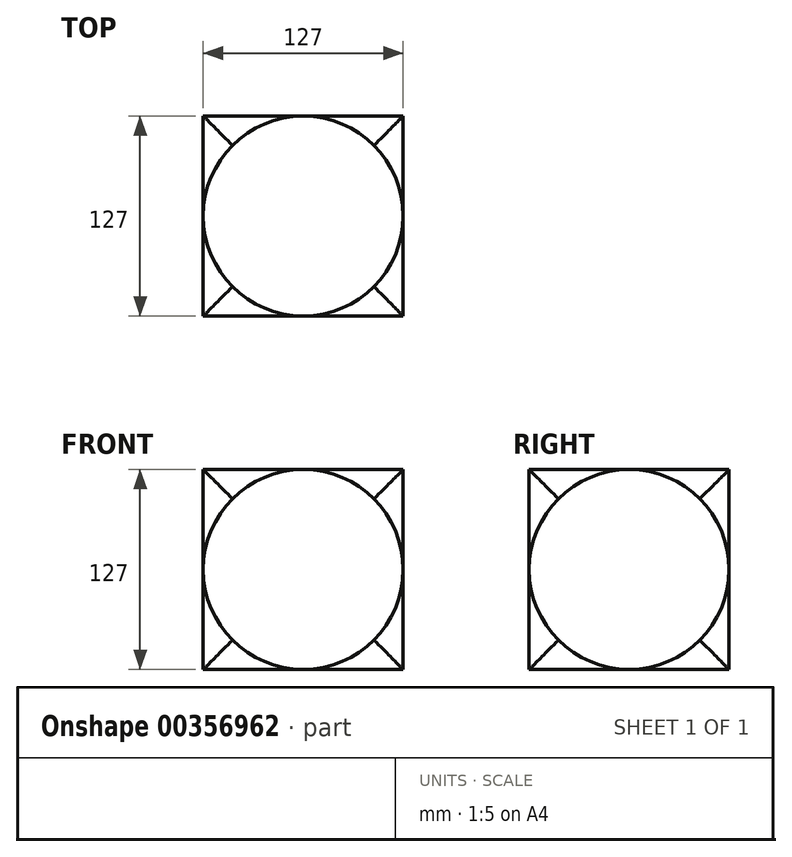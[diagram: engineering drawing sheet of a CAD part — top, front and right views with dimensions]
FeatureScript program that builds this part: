
annotation { "Feature Type Name" : "Feature", "Feature Type Description" : "" }
export const myFeature = defineFeature(function(context is Context, id is Id, definition is map)
    precondition{}
    {
        {
            var Q0;
            Q0=qCreatedBy(makeId("Front.planeOp"),FACE);
            var sketch = newSketch(context, id + "F0", { "sketchPlane" : qUnion([Q0])});
            skCircle(sketch, "E0", {"center": v(0, 0) * mm, "radius": 63.5 * mm});
            skSolve(sketch);
        }
        {
            var Q0;
            Q0 = qSketchRegion(id + "F0", true);
            extrude(context, id + "F1", {"entities" : qUnion([Q0]), "depth" : 63.5 * mm, "hasSecondDirection" : true, "secondDirectionOppositeDirection" : true, "secondDirectionDepth" : 63.5 * mm});
        }
        {
            var Q0;
            Q0=qCreatedBy(makeId("Top.planeOp"),FACE);
            var sketch = newSketch(context, id + "F2", { "sketchPlane" : qUnion([Q0])});
            skCircle(sketch, "E1", {"center": v(0, 0) * mm, "radius": 63.5 * mm});
            skSolve(sketch);
        }
        {
            var Q0;
            Q0 = qSketchRegion(id + "F2", true);
            extrude(context, id + "F3", {"entities" : qUnion([Q0]), "operationType" : NewBodyOperationType.ADD, "depth" : 63.5 * mm, "hasSecondDirection" : true, "secondDirectionOppositeDirection" : true, "secondDirectionDepth" : 63.5 * mm});
        }
        {
            var Q0;
            Q0=qCreatedBy(makeId("Right.planeOp"),FACE);
            var sketch = newSketch(context, id + "F4", { "sketchPlane" : qUnion([Q0])});
            skCircle(sketch, "E2", {"center": v(0, 0) * mm, "radius": 63.5 * mm});
            skSolve(sketch);
        }
        {
            var Q0;
            Q0 = qSketchRegion(id + "F4", true);
            extrude(context, id + "F5", {"entities" : qUnion([Q0]), "operationType" : NewBodyOperationType.ADD, "depth" : 63.5 * mm, "hasSecondDirection" : true, "secondDirectionOppositeDirection" : true, "secondDirectionDepth" : 63.5 * mm});
        }
    });
